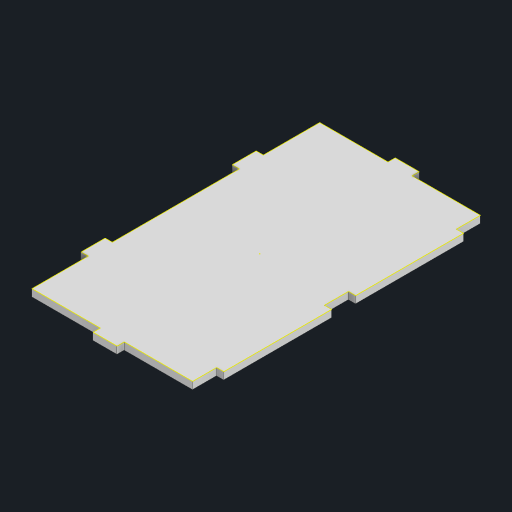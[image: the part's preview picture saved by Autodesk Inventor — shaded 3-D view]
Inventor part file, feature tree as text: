
AUTODESK INVENTOR PART (.ipt)
format: ipt  version: 2023 (Build 270158000, 158)  size: 159,232 bytes
history: native  units: mm
features: sketch x5, extrude x4, projected_geometry x1
ambient origin geometry x8: Origin, YZ Plane, XZ Plane, XY Plane, X Axis, Y Axis, Z Axis, Center Point
bodies: Solid1 (feature_tree)
feature tree (10):
  extrude  "Extrusion1"  Depth=120.0mm
  extrude  "Extrusion2"  Depth=3.0mm
  extrude  "Extrusion3"  Depth=3.0mm
  extrude  "Extrusion4"  Depth=10.0mm
  sketch  "Sketch5"  dims[d9=0.0mm d10=0.0mm d15=10.0mm d16=3.0mm d17=10.0mm d18=3.0mm d19=3.0mm d20=0.0mm d21=10.0mm d22=10.0mm d23=3.0mm d24=10.0mm d25=3.0mm d26=10.0mm d27=126.0mm d28=31.5mm d29=31.5mm d30=3.0mm d31=0.0mm]
  sketch  "Sketch1"  dims[d0=70.0mm d1=120.0mm]
  sketch  "Sketch2"  dims[d2=3.0mm d3=0.0mm d4=3.0mm]
  sketch  "Sketch3"  dims[d5=10.0mm d6=3.0mm]
  sketch  "Sketch4"  dims[d7=10.0mm d8=10.0mm]
  projected_geometry  "Project Cut Edges1"
